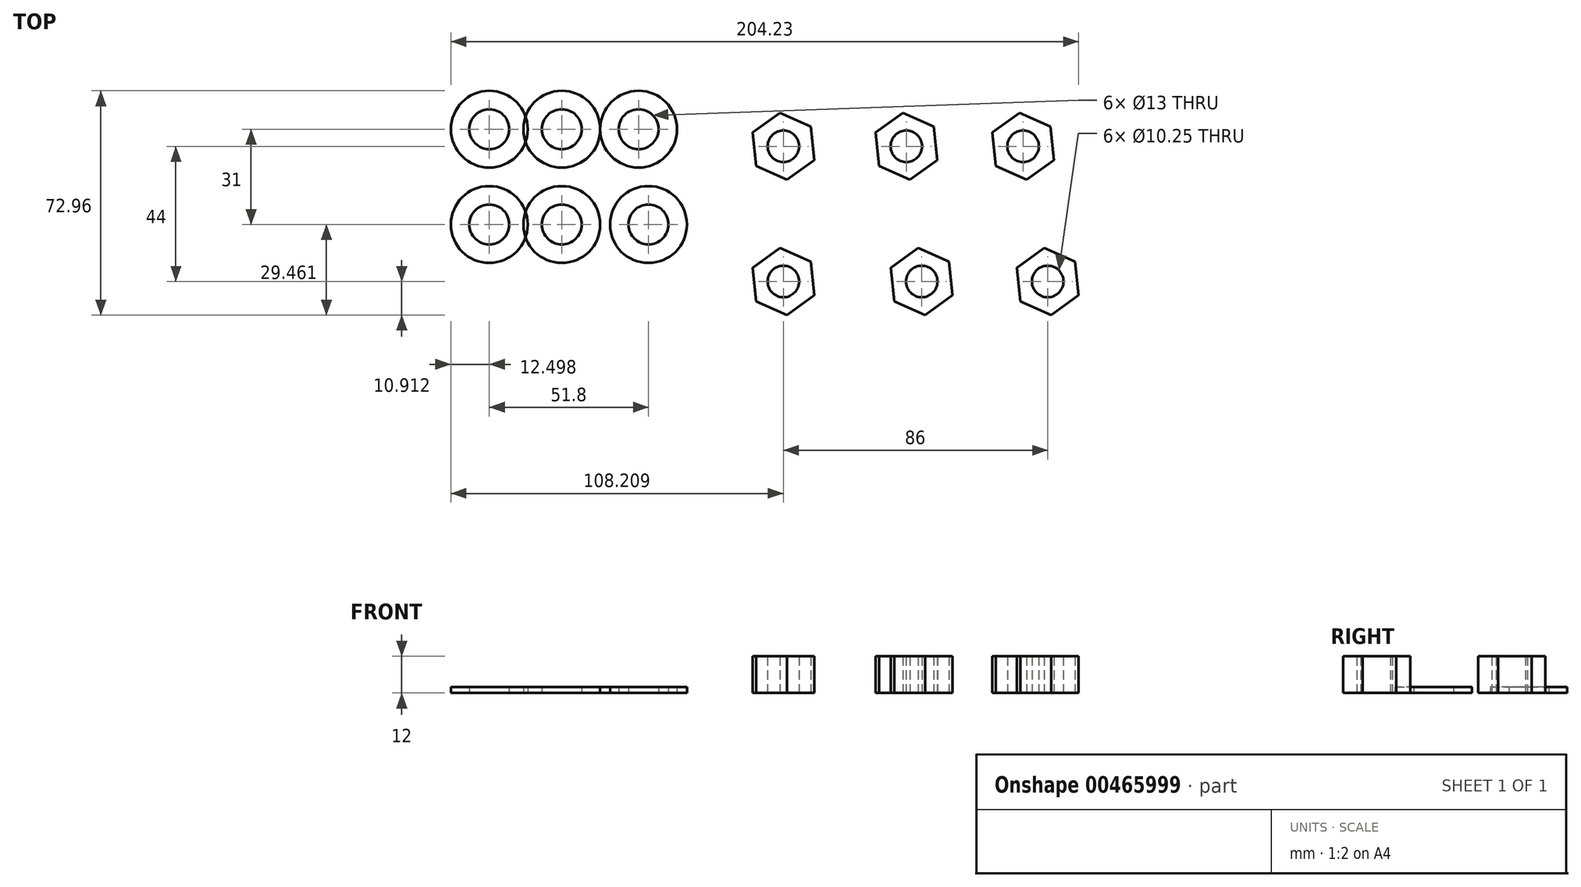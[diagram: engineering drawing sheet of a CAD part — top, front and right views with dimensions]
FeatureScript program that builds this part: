
annotation { "Feature Type Name" : "Feature", "Feature Type Description" : "" }
export const myFeature = defineFeature(function(context is Context, id is Id, definition is map)
    precondition{}
    {
        {
            var Q0;
            Q0=qCreatedBy(makeId("Top.planeOp"),FACE);
            var sketch = newSketch(context, id + "F0", { "sketchPlane" : qUnion([Q0])});
            skCircle(sketch, "E0", {"center": v(-126.14, 20.37) * mm, "radius": 6.5 * mm});
            skCircle(sketch, "E1", {"center": v(-126.14, 20.37) * mm, "radius": 12.5 * mm});
            skSolve(sketch);
        }
        {
            var Q0;
            Q0=makeQuery(id+"F0.imprint","IMPRINT",FACE,{"disambiguationData":[TD([[makeQuery(id+"F0.imprint","IMPRINT",EDGE,{"derivedFrom":sQuery(id+"F0.wireOp",EDGE,"E0")}),-1.0]])]});
            extrude(context, id + "F1", {"entities" : qUnion([Q0]), "depth" : 2 * mm});
        }
        {
            var Q0;
            Q0=makeQuery(id+"F1.opExtrude","SWEPT_BODY",BODY,{"disambiguationData":[OSD([sQuery(id+"F0.wireOp",EDGE,"E0"),sQuery(id+"F0.wireOp",EDGE,"E1")])]});
            transform(context, id + "F2", {"entities" : qUnion([Q0]), "transformType" : TransformType.TRANSLATION_3D, "dx" : 23.6 * mm, "dy" : 0 * mm, "dz" : 0 * mm, "makeCopy" : true});
        }
        {
            var Q0;
            Q0=makeQuery(id+"F1.opExtrude","SWEPT_BODY",BODY,{"disambiguationData":[OSD([sQuery(id+"F0.wireOp",EDGE,"E0"),sQuery(id+"F0.wireOp",EDGE,"E1")])]});
            transform(context, id + "F3", {"entities" : qUnion([Q0]), "transformType" : TransformType.TRANSLATION_3D, "dx" : 0 * mm, "dy" : 31 * mm, "dz" : 0 * mm, "makeCopy" : true});
        }
        {
            var Q0;
            Q0=makeQuery(id+"F2.opPattern","COPY",BODY,{"derivedFrom":makeQuery(id+"F1.opExtrude","SWEPT_BODY",BODY,{"disambiguationData":[OSD([sQuery(id+"F0.wireOp",EDGE,"E0"),sQuery(id+"F0.wireOp",EDGE,"E1")])]}),"instanceName":"1"});
            transform(context, id + "F4", {"entities" : qUnion([Q0]), "transformType" : TransformType.TRANSLATION_3D, "dx" : 0 * mm, "dy" : 31 * mm, "dz" : 0 * mm, "makeCopy" : true});
        }
        {
            var Q0;
            Q0=makeQuery(id+"F4.opPattern","COPY",BODY,{"derivedFrom":makeQuery(id+"F2.opPattern","COPY",BODY,{"derivedFrom":makeQuery(id+"F1.opExtrude","SWEPT_BODY",BODY,{"disambiguationData":[OSD([sQuery(id+"F0.wireOp",EDGE,"E0"),sQuery(id+"F0.wireOp",EDGE,"E1")])]}),"instanceName":"1"}),"instanceName":"1"});
            transform(context, id + "F5", {"entities" : qUnion([Q0]), "transformType" : TransformType.TRANSLATION_3D, "dx" : 25 * mm, "dy" : 0 * mm, "dz" : 0 * mm, "makeCopy" : true});
        }
        {
            var Q0;
            Q0=makeQuery(id+"F2.opPattern","COPY",BODY,{"derivedFrom":makeQuery(id+"F1.opExtrude","SWEPT_BODY",BODY,{"disambiguationData":[OSD([sQuery(id+"F0.wireOp",EDGE,"E0"),sQuery(id+"F0.wireOp",EDGE,"E1")])]}),"instanceName":"1"});
            transform(context, id + "F6", {"entities" : qUnion([Q0]), "transformType" : TransformType.TRANSLATION_3D, "dx" : 28.2 * mm, "dy" : 0 * mm, "dz" : 0 * mm, "makeCopy" : true});
        }
        {
            var Q0;
            Q0=qCreatedBy(makeId("Top.planeOp"),FACE);
            var sketch = newSketch(context, id + "F7", { "sketchPlane" : qUnion([Q0])});
            skCircle(sketch, "E2.cCircle", {"center": v(-30.43, 45.82) * mm, "radius": 9.5 * mm, "construction": true});
            skLineSegment(sketch, "E2.0", {"start": v(-20.41, 41.35) * mm, "end": v(-29.3, 34.91) * mm});
            skLineSegment(sketch, "E2.1", {"start": v(-29.3, 34.91) * mm, "end": v(-39.31, 39.38) * mm});
            skLineSegment(sketch, "E2.2", {"start": v(-39.31, 39.38) * mm, "end": v(-40.45, 50.3) * mm});
            skLineSegment(sketch, "E2.3", {"start": v(-40.45, 50.3) * mm, "end": v(-31.57, 56.73) * mm});
            skLineSegment(sketch, "E2.4", {"start": v(-31.57, 56.73) * mm, "end": v(-21.55, 52.26) * mm});
            skLineSegment(sketch, "E2.5", {"start": v(-21.55, 52.26) * mm, "end": v(-20.41, 41.35) * mm});
            skPoint(sketch, "E2.0.midPoint", {"position": v(-24.85, 38.13) * mm});
            skCircle(sketch, "E3", {"center": v(-30.43, 45.82) * mm, "radius": 5.12 * mm});
            skSolve(sketch);
        }
        {
            var Q0;
            Q0 = qSketchRegion(id + "F7", true);
            extrude(context, id + "F8", {"entities" : qUnion([Q0]), "depth" : 12 * mm});
        }
        {
            var Q0;
            Q0=makeQuery(id+"F8.opExtrude","SWEPT_BODY",BODY,{"disambiguationData":[OSD([sQuery(id+"F7.wireOp",EDGE,"E2.0"),sQuery(id+"F7.wireOp",EDGE,"E2.1"),sQuery(id+"F7.wireOp",EDGE,"E2.2"),sQuery(id+"F7.wireOp",EDGE,"E2.3"),sQuery(id+"F7.wireOp",EDGE,"E2.4"),sQuery(id+"F7.wireOp",EDGE,"E2.5"),sQuery(id+"F7.wireOp",EDGE,"E3")])]});
            transform(context, id + "F9", {"entities" : qUnion([Q0]), "transformType" : TransformType.TRANSLATION_3D, "dx" : 0 * mm, "dy" : -44 * mm, "dz" : 0 * mm, "makeCopy" : true});
        }
        {
            var Q0;
            Q0=makeQuery(id+"F9.opPattern","COPY",BODY,{"derivedFrom":makeQuery(id+"F8.opExtrude","SWEPT_BODY",BODY,{"disambiguationData":[OSD([sQuery(id+"F7.wireOp",EDGE,"E2.0"),sQuery(id+"F7.wireOp",EDGE,"E2.1"),sQuery(id+"F7.wireOp",EDGE,"E2.2"),sQuery(id+"F7.wireOp",EDGE,"E2.3"),sQuery(id+"F7.wireOp",EDGE,"E2.4"),sQuery(id+"F7.wireOp",EDGE,"E2.5"),sQuery(id+"F7.wireOp",EDGE,"E3")])]}),"instanceName":"1"});
            transform(context, id + "F10", {"entities" : qUnion([Q0]), "transformType" : TransformType.TRANSLATION_3D, "dx" : 45 * mm, "dy" : 0 * mm, "dz" : 0 * mm, "makeCopy" : true});
        }
        {
            var Q0;
            Q0=makeQuery(id+"F8.opExtrude","SWEPT_BODY",BODY,{"disambiguationData":[OSD([sQuery(id+"F7.wireOp",EDGE,"E2.0"),sQuery(id+"F7.wireOp",EDGE,"E2.1"),sQuery(id+"F7.wireOp",EDGE,"E2.2"),sQuery(id+"F7.wireOp",EDGE,"E2.3"),sQuery(id+"F7.wireOp",EDGE,"E2.4"),sQuery(id+"F7.wireOp",EDGE,"E2.5"),sQuery(id+"F7.wireOp",EDGE,"E3")])]});
            transform(context, id + "F11", {"entities" : qUnion([Q0]), "transformType" : TransformType.TRANSLATION_3D, "dx" : 40 * mm, "dy" : 0 * mm, "dz" : 0 * mm, "makeCopy" : true});
        }
        {
            var Q0;
            Q0=makeQuery(id+"F10.opPattern","COPY",BODY,{"derivedFrom":makeQuery(id+"F9.opPattern","COPY",BODY,{"derivedFrom":makeQuery(id+"F8.opExtrude","SWEPT_BODY",BODY,{"disambiguationData":[OSD([sQuery(id+"F7.wireOp",EDGE,"E2.0"),sQuery(id+"F7.wireOp",EDGE,"E2.1"),sQuery(id+"F7.wireOp",EDGE,"E2.2"),sQuery(id+"F7.wireOp",EDGE,"E2.3"),sQuery(id+"F7.wireOp",EDGE,"E2.4"),sQuery(id+"F7.wireOp",EDGE,"E2.5"),sQuery(id+"F7.wireOp",EDGE,"E3")])]}),"instanceName":"1"}),"instanceName":"1"});
            transform(context, id + "F12", {"entities" : qUnion([Q0]), "transformType" : TransformType.TRANSLATION_3D, "dx" : 41 * mm, "dy" : 0 * mm, "dz" : 0 * mm, "makeCopy" : true});
        }
        {
            var Q0;
            Q0=makeQuery(id+"F11.opPattern","COPY",BODY,{"derivedFrom":makeQuery(id+"F8.opExtrude","SWEPT_BODY",BODY,{"disambiguationData":[OSD([sQuery(id+"F7.wireOp",EDGE,"E2.0"),sQuery(id+"F7.wireOp",EDGE,"E2.1"),sQuery(id+"F7.wireOp",EDGE,"E2.2"),sQuery(id+"F7.wireOp",EDGE,"E2.3"),sQuery(id+"F7.wireOp",EDGE,"E2.4"),sQuery(id+"F7.wireOp",EDGE,"E2.5"),sQuery(id+"F7.wireOp",EDGE,"E3")])]}),"instanceName":"1"});
            transform(context, id + "F13", {"entities" : qUnion([Q0]), "transformType" : TransformType.TRANSLATION_3D, "dx" : 38 * mm, "dy" : 0 * mm, "dz" : 0 * mm, "makeCopy" : true});
        }
    });
